# Revit family: Haworth_XSeries_Locker_GroupTriple
name_source: partatom
category: Furniture Systems
units: mm (PartAtom-declared; Revit-internal decimal feet)

## family parameters
Always vertical = Yes
Cut with Voids When Loaded = No
OmniClass Number = 23.40.70.14.64.21
OmniClass Title = Systems Furniture
Part Type = Normal
Room Calculation Point = No
Round Connector Dimension = Use Diameter
Shared = No
Work Plane-Based = No

## types (3) — shared parameters
Actual Depth = 18 3/4"
Actual Width = 36"
Assembly Code = E2020200
Base Height = 1 7/8"
Classic Pull = No
Crescent Pull = No
Custom Depth = No
Custom Height = No
Custom Size = No
Custom Width = No
Depth = 18 3/4"
Description = Haworth XSeries Locker - Group Triple
Door Offset = 1/16"
Door Width = 11 13/16"
J Pull = No
Linear Pull = Yes
Manufacturer = Haworth
Max. Depth = 18 3/4"
Max. Height = 63 1/2"
Max. Width = 36"
Min. Depth = 18 3/4"
Min. Height = 39 1/2"
Min. Width = 36"
Model = JA18-5136
Panel Thickness = 3/4"
Panel Thickness Half = 3/8"
Pull Ellipse = No
Pull Finish = Haworth _ Metal _ Brushed Aluminum
Pull Offset Centerline = 10 1/2"
Radius Pull = No
Revision Number = 2
Size = Verify Final Dim. w/ Haworth
Standard Depths = 18.75 in.
Standard Heights = 39.5, 51.5, 63.5 in.
Standard Widths = 36 in.
Sustainability Info = https://www.haworth.com
Taper Pull = No
Top Height = 1 1/4"
URL = http://www.haworth.com
URL - Product = https://www.haworth.com
Warranty = https://cdn.shopify.com
Width = 36"

## per-type parameters (varying)
| type | Actual Height | Door Height | Height | Pull Height |
| 18d 36w 51h | 51 1/2" | 48 1/4" | 51 1/2" | 24 1/8" |
| 18d 36w 39h | 39 1/2" | 36 1/4" | 39 1/2" | 18 1/8" |
| 18d 36w 63h | 63 1/2" | 60 1/4" | 63 1/2" | 30 1/8" |

## geometry (parser evidence)
native form markers: Sweep x7
no freeform markers — native parametric forms only
